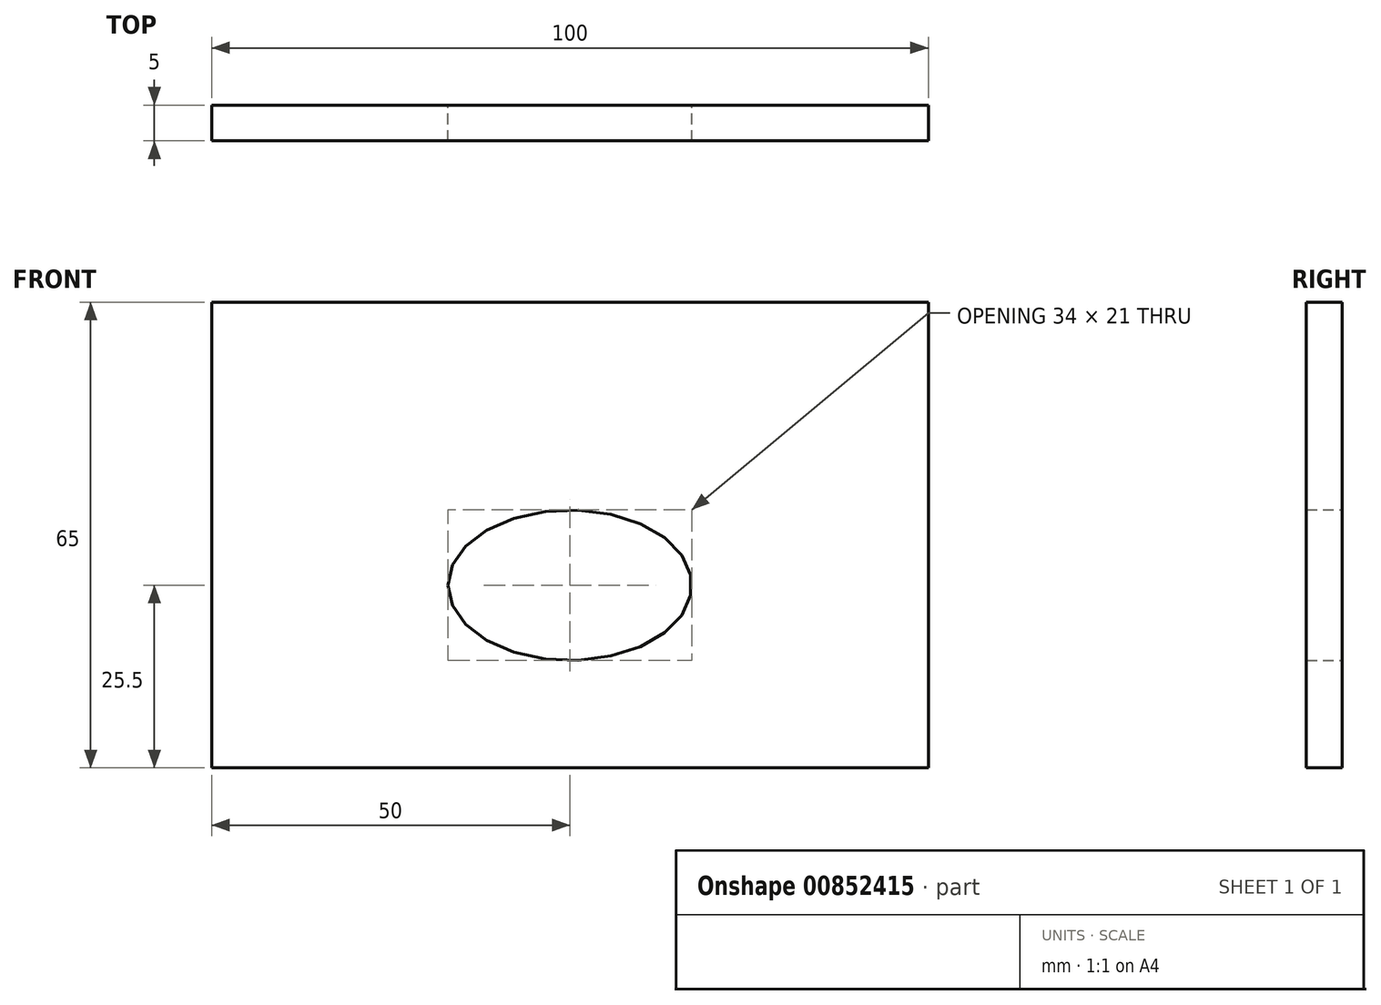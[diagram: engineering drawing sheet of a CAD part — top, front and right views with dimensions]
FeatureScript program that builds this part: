
annotation { "Feature Type Name" : "Feature", "Feature Type Description" : "" }
export const myFeature = defineFeature(function(context is Context, id is Id, definition is map)
    precondition{}
    {
        {
            var Q0;
            Q0=qCreatedBy(makeId("Front.planeOp"),FACE);
            var sketch = newSketch(context, id + "F0", { "sketchPlane" : qUnion([Q0])});
            skEllipse(sketch, "E0", {"center": v(0, 0) * mm, "majorRadius": 17 * mm, "minorRadius": 10.5 * mm, "majorAxis": v(-1, 0)});
            skLineSegment(sketch, "E1", {"start": v(0, 10.5) * mm, "end": v(0, 39.5) * mm});
            skLineSegment(sketch, "E2", {"start": v(0, 39.5) * mm, "end": v(50, 39.5) * mm});
            skLineSegment(sketch, "E3", {"start": v(0, 39.5) * mm, "end": v(-50, 39.5) * mm});
            skLineSegment(sketch, "E4", {"start": v(-50, 39.5) * mm, "end": v(-50, -25.5) * mm});
            skLineSegment(sketch, "E5", {"start": v(-50, -25.5) * mm, "end": v(50, -25.5) * mm});
            skLineSegment(sketch, "E6", {"start": v(50, -25.5) * mm, "end": v(50, 39.5) * mm});
            skSolve(sketch);
        }
        {
            var Q0;
            Q0=makeQuery(id+"F0.imprint","IMPRINT",FACE,{"disambiguationData":[TD([[makeQuery(id+"F0.imprint","IMPRINT",EDGE,{"derivedFrom":sQuery(id+"F0.wireOp",EDGE,"7iOlp8eU-noiV-VMPf-KDUT-vSvCykkrHX22")}),1.0]])]});
            var Q1;
            Q1=makeQuery(id+"F0.imprint","IMPRINT",FACE,{"disambiguationData":[TD([[makeQuery(id+"F0.imprint","IMPRINT",EDGE,{"derivedFrom":sQuery(id+"F0.wireOp",EDGE,"E0")}),-1.0]])]});
            extrude(context, id + "F1", {"entities" : qUnion([Q0, Q1]), "depth" : 5 * mm, "offsetDistance" : 25 * mm});
        }
    });
